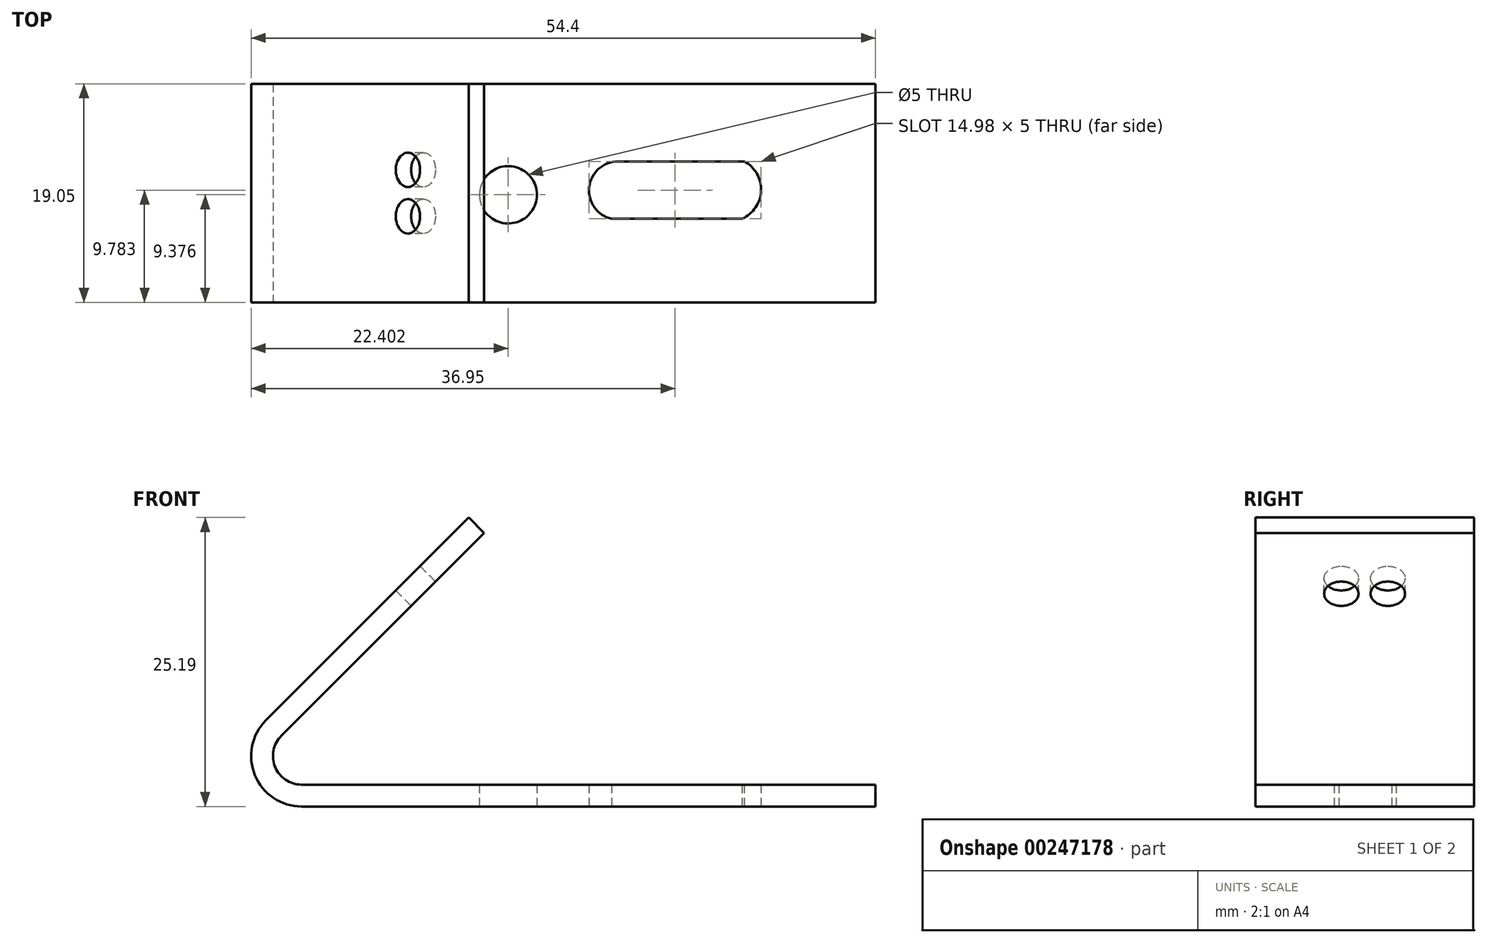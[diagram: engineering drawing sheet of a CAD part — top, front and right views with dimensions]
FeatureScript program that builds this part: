
annotation { "Feature Type Name" : "Feature", "Feature Type Description" : "" }
export const myFeature = defineFeature(function(context is Context, id is Id, definition is map)
    precondition{}
    {
        {
            var Q0;
            Q0=qCreatedBy(makeId("Front.planeOp"),FACE);
            var sketch = newSketch(context, id + "F0", { "sketchPlane" : qUnion([Q0])});
            skLineSegment(sketch, "E0", {"start": v(6.25, 0) * mm, "end": v(-43.75, 0) * mm});
            skLineSegment(sketch, "E1", {"start": v(-46.86, 7.51) * mm, "end": v(-29.18, 25.19) * mm});
            skPoint(sketch, "E2.visualSharp", {"position": v(-54.37, 0) * mm});
            skArc(sketch, "E2.filletArc", {"start": v(-46.86, 7.51) * mm, "mid": v(-47.81, 2.72) * mm, "end": v(-43.75, 0) * mm});
            skLineSegment(sketch, "E3.0", {"start": v(-45.52, 6.17) * mm, "end": v(-27.84, 23.85) * mm});
            skArc(sketch, "E3.1", {"start": v(-45.52, 6.17) * mm, "mid": v(-46.06, 3.44) * mm, "end": v(-43.75, 1.9) * mm});
            skLineSegment(sketch, "E3.2", {"start": v(6.25, 1.9) * mm, "end": v(-43.75, 1.9) * mm});
            skLineSegment(sketch, "E4", {"start": v(-29.18, 25.19) * mm, "end": v(-27.84, 23.85) * mm});
            skLineSegment(sketch, "E5", {"start": v(6.25, 1.9) * mm, "end": v(6.25, 0) * mm});
            skSolve(sketch);
        }
        {
            var Q0;
            Q0 = qSketchRegion(id + "F0", true);
            extrude(context, id + "F1", {"entities" : qUnion([Q0]), "oppositeDirection" : true, "depth" : 19.05 * mm});
        }
        {
            var Q0;
            Q0=makeQuery(id+"F1.opExtrude","SWEPT_FACE",FACE,{"disambiguationData":[OSD([sQuery(id+"F0.wireOp",EDGE,"E1")])]});
            var sketch = newSketch(context, id + "F2", { "sketchPlane" : qUnion([Q0])});
            skCircle(sketch, "E6", {"center": v(-11.55, -10.32) * mm, "radius": 1.5 * mm});
            skCircle(sketch, "E7", {"center": v(-7.5, -10.32) * mm, "radius": 1.5 * mm});
            skSolve(sketch);
        }
        {
            var Q0;
            Q0=makeQuery(id+"F2.imprint","IMPRINT",FACE,{"disambiguationData":[TD([[makeQuery(id+"F2.imprint","IMPRINT",EDGE,{"derivedFrom":sQuery(id+"F2.wireOp",EDGE,"E7")}),1.0]])]});
            var Q1;
            Q1=makeQuery(id+"F2.imprint","IMPRINT",FACE,{"disambiguationData":[TD([[makeQuery(id+"F2.imprint","IMPRINT",EDGE,{"derivedFrom":sQuery(id+"F2.wireOp",EDGE,"E6")}),1.0]])]});
            var Q2;
            Q2=sQuery(id+"F2.wireOp",EDGE,"E7");
            extrude(context, id + "F3", {"entities" : qUnion([Q0, Q1]), "operationType" : NewBodyOperationType.REMOVE, "surfaceEntities" : qUnion([Q2]), "oppositeDirection" : true, "depth" : 12.7 * mm});
        }
        {
            var Q0;
            Q0=makeQuery(id+"F1.opExtrude","SWEPT_FACE",FACE,{"disambiguationData":[OSD([sQuery(id+"F0.wireOp",EDGE,"E0")])]});
            var sketch = newSketch(context, id + "F4", { "sketchPlane" : qUnion([Q0])});
            skCircle(sketch, "E8", {"center": v(-25.75, -9.38) * mm, "radius": 2.5 * mm});
            skLineSegment(sketch, "E9", {"start": v(-16.73, -7.28) * mm, "end": v(-5.37, -7.28) * mm});
            skLineSegment(sketch, "E10", {"start": v(-16.18, -12.28) * mm, "end": v(-5.16, -12.28) * mm});
            skArc(sketch, "E11", {"start": v(-5.16, -12.28) * mm, "mid": v(-3.7, -9.72) * mm, "end": v(-5.37, -7.28) * mm});
            skArc(sketch, "E12", {"start": v(-16.73, -7.28) * mm, "mid": v(-18.7, -10.03) * mm, "end": v(-16.18, -12.28) * mm});
            skSolve(sketch);
        }
        {
            var Q0;
            Q0=makeQuery(id+"F4.imprint","IMPRINT",FACE,{"disambiguationData":[TD([[makeQuery(id+"F4.imprint","IMPRINT",EDGE,{"derivedFrom":sQuery(id+"F4.wireOp",EDGE,"E9")}),-1.0]])]});
            var Q1;
            Q1=makeQuery(id+"F4.imprint","IMPRINT",FACE,{"disambiguationData":[TD([[makeQuery(id+"F4.imprint","IMPRINT",EDGE,{"derivedFrom":sQuery(id+"F4.wireOp",EDGE,"E8")}),1.0]])]});
            extrude(context, id + "F5", {"entities" : qUnion([Q0, Q1]), "operationType" : NewBodyOperationType.REMOVE, "oppositeDirection" : true, "depth" : 12.7 * mm});
        }
    });
